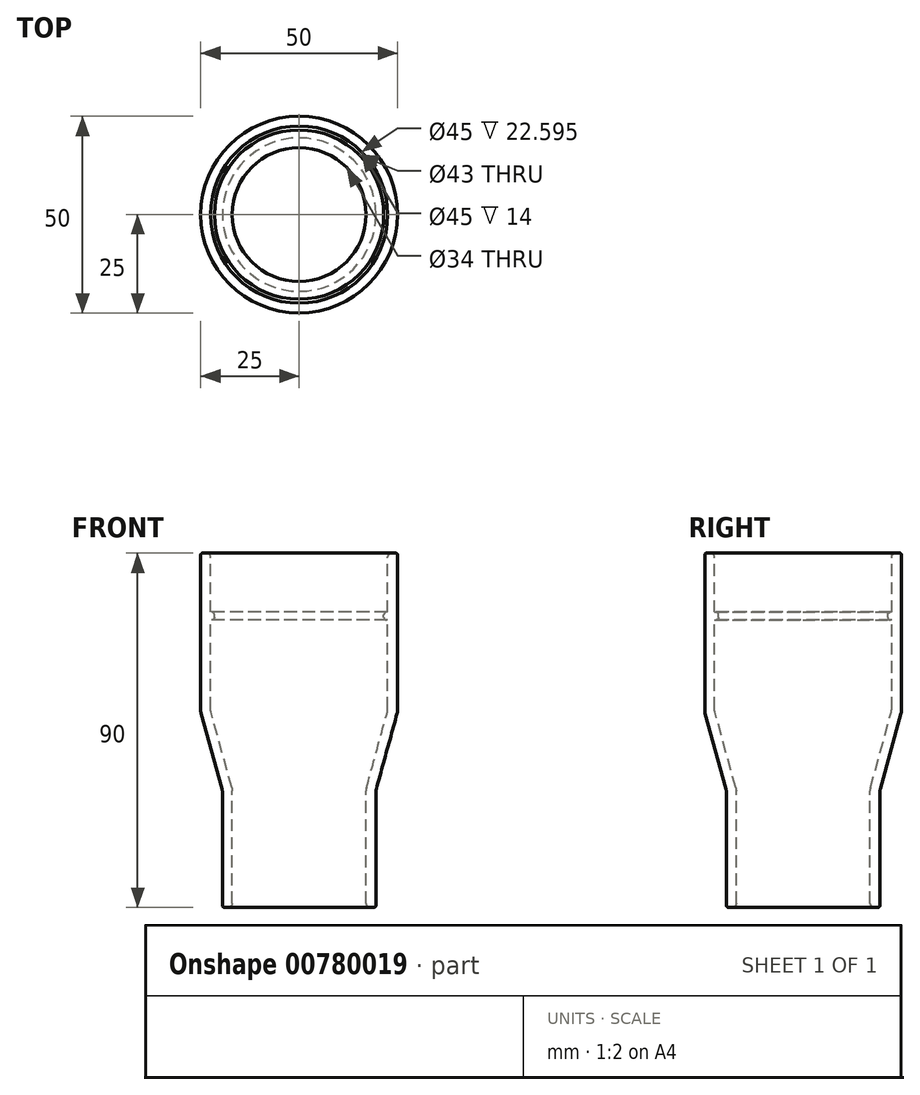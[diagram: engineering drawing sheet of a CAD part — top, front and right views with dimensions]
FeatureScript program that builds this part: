
annotation { "Feature Type Name" : "Feature", "Feature Type Description" : "" }
export const myFeature = defineFeature(function(context is Context, id is Id, definition is map)
    precondition{}
    {
        {
            var Q0;
            Q0=qCreatedBy(makeId("Front.planeOp"),FACE);
            var sketch = newSketch(context, id + "F0", { "sketchPlane" : qUnion([Q0])});
            skLineSegment(sketch, "E0", {"start": v(-22.5, 25.49) * mm, "end": v(-22.5, -13.1) * mm});
            skLineSegment(sketch, "E1", {"start": v(-22.4, -13.9) * mm, "end": v(-17.1, -33.12) * mm});
            skLineSegment(sketch, "E2", {"start": v(-17, -33.92) * mm, "end": v(-17, -62.51) * mm});
            skLineSegment(sketch, "E3", {"start": v(0, 0) * mm, "end": v(0, -99.32) * mm, "construction": true});
            skPoint(sketch, "E4", {"position": v(-22.5, 11.49) * mm});
            skPoint(sketch, "E5", {"position": v(-22.5, 9.49) * mm});
            skLineSegment(sketch, "E6", {"start": v(-22.5, 11.49) * mm, "end": v(-22.2, 11.49) * mm});
            skLineSegment(sketch, "E7", {"start": v(-21.5, 10.79) * mm, "end": v(-21.5, 10.19) * mm});
            skLineSegment(sketch, "E8", {"start": v(-22.2, 9.49) * mm, "end": v(-22.5, 9.49) * mm});
            skLineSegment(sketch, "E9.0", {"start": v(-19.5, -34.25) * mm, "end": v(-19.5, -63.01) * mm});
            skLineSegment(sketch, "E9.1", {"start": v(-24.9, -14.24) * mm, "end": v(-19.6, -33.46) * mm});
            skLineSegment(sketch, "E9.2", {"start": v(-25, 25.99) * mm, "end": v(-25, -13.44) * mm});
            skLineSegment(sketch, "E10", {"start": v(-24.5, 26.49) * mm, "end": v(-23.5, 26.49) * mm});
            skLineSegment(sketch, "E11", {"start": v(-19, -63.51) * mm, "end": v(-18, -63.51) * mm});
            skPoint(sketch, "E12.visualSharp", {"position": v(-22.5, 26.49) * mm});
            skArc(sketch, "E12.filletArc", {"start": v(-22.5, 25.49) * mm, "mid": v(-22.8, 26.2) * mm, "end": v(-23.5, 26.49) * mm});
            skPoint(sketch, "E13.visualSharp", {"position": v(-17, -63.51) * mm});
            skArc(sketch, "E13.filletArc", {"start": v(-18, -63.51) * mm, "mid": v(-17.3, -63.22) * mm, "end": v(-17, -62.51) * mm});
            skPoint(sketch, "E14.visualSharp", {"position": v(-25, 26.49) * mm});
            skArc(sketch, "E14.filletArc", {"start": v(-24.5, 26.49) * mm, "mid": v(-24.85, 26.34) * mm, "end": v(-25, 25.99) * mm});
            skPoint(sketch, "E15.visualSharp", {"position": v(-19.5, -63.51) * mm});
            skArc(sketch, "E15.filletArc", {"start": v(-19.5, -63.01) * mm, "mid": v(-19.35, -63.37) * mm, "end": v(-19, -63.51) * mm});
            skPoint(sketch, "E16.visualSharp", {"position": v(-25, -13.85) * mm});
            skArc(sketch, "E16.filletArc", {"start": v(-25, -13.44) * mm, "mid": v(-24.97, -13.85) * mm, "end": v(-24.9, -14.24) * mm});
            skPoint(sketch, "E17.visualSharp", {"position": v(-19.5, -33.85) * mm});
            skArc(sketch, "E17.filletArc", {"start": v(-19.5, -34.25) * mm, "mid": v(-19.53, -33.85) * mm, "end": v(-19.6, -33.46) * mm});
            skPoint(sketch, "E18.visualSharp", {"position": v(-17, -33.51) * mm});
            skArc(sketch, "E18.filletArc", {"start": v(-17, -33.92) * mm, "mid": v(-17.03, -33.52) * mm, "end": v(-17.1, -33.12) * mm});
            skPoint(sketch, "E19.visualSharp", {"position": v(-22.5, -13.51) * mm});
            skArc(sketch, "E19.filletArc", {"start": v(-22.5, -13.1) * mm, "mid": v(-22.47, -13.5) * mm, "end": v(-22.4, -13.9) * mm});
            skPoint(sketch, "E20.visualSharp", {"position": v(-21.5, 11.49) * mm});
            skArc(sketch, "E20.filletArc", {"start": v(-21.5, 10.79) * mm, "mid": v(-21.7, 11.28) * mm, "end": v(-22.2, 11.49) * mm});
            skPoint(sketch, "E21.visualSharp", {"position": v(-21.5, 9.49) * mm});
            skArc(sketch, "E21.filletArc", {"start": v(-22.2, 9.49) * mm, "mid": v(-21.7, 9.7) * mm, "end": v(-21.5, 10.19) * mm});
            skSolve(sketch);
        }
        {
            var Q0;
            {var subQ0=sQuery(id+"F0.wireOp",EDGE,"E1");Q0=makeQuery(id+"F0.imprint","IMPRINT",FACE,{"disambiguationData":[TD([[makeQuery(id+"F0.imprint","IMPRINT",EDGE,{"derivedFrom":subQ0}),-1.0]])]});}
            var Q1;
            {var subQ0=sQuery(id+"F0.wireOp",EDGE,"E6");Q1=makeQuery(id+"F0.imprint","IMPRINT",FACE,{"disambiguationData":[TD([[makeQuery(id+"F0.imprint","IMPRINT",EDGE,{"derivedFrom":subQ0}),-1.0]])]});}
            var Q2;
            Q2=sQuery(id+"F0.wireOp",EDGE,"E3");
            revolve(context, id + "F1", {"surfaceOperationType" : NewSurfaceOperationType.NEW, "entities" : qUnion([Q0, Q1]), "axis" : qUnion([Q2]), "revolveType" : RevolveType.FULL});
        }
    });
